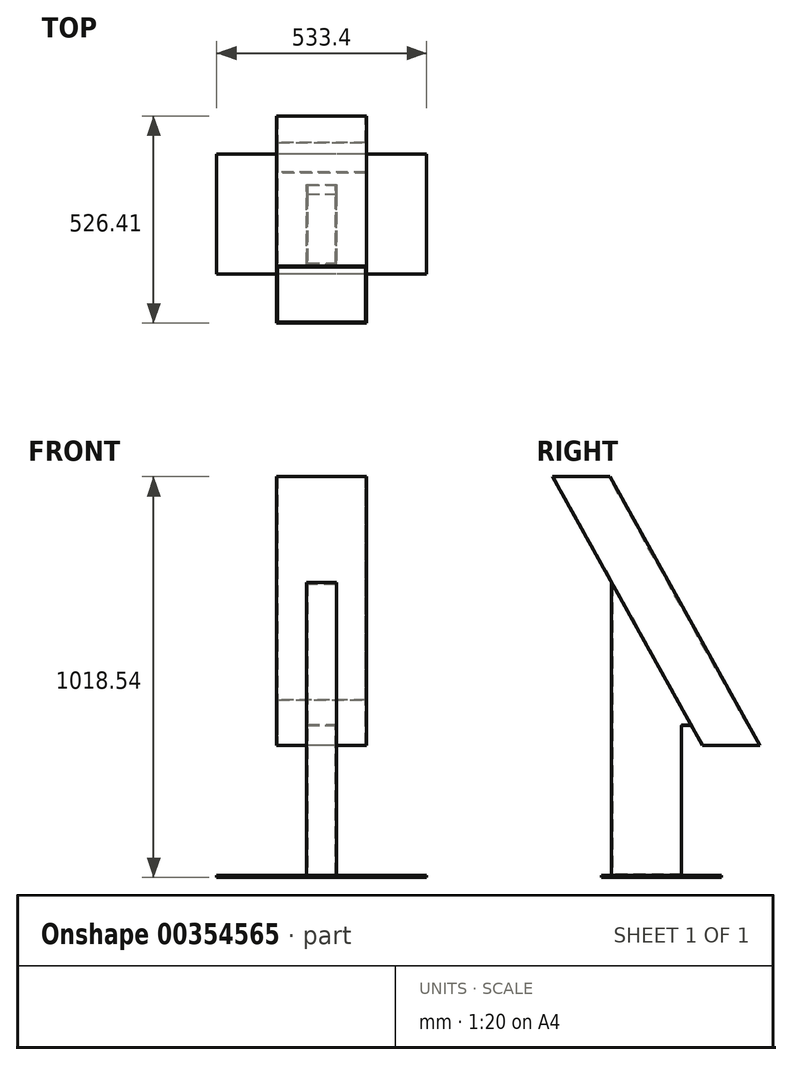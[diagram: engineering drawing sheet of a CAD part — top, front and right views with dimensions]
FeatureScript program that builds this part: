
annotation { "Feature Type Name" : "Feature", "Feature Type Description" : "" }
export const myFeature = defineFeature(function(context is Context, id is Id, definition is map)
    precondition{}
    {
        {
            var Q0;
            Q0=qCreatedBy(makeId("Right.planeOp"),FACE);
            var sketch = newSketch(context, id + "F0", { "sketchPlane" : qUnion([Q0])});
            skLineSegment(sketch, "E0", {"start": v(0, 0) * mm, "end": v(145.41, 0) * mm});
            skLineSegment(sketch, "E1", {"start": v(145.41, 0) * mm, "end": v(-235.59, 683.26) * mm});
            skLineSegment(sketch, "E2", {"start": v(-235.59, 683.26) * mm, "end": v(-381, 683.26) * mm});
            skLineSegment(sketch, "E3", {"start": v(-381, 683.26) * mm, "end": v(0, 0) * mm});
            skSolve(sketch);
        }
        {
            var Q0;
            Q0=makeQuery(id+"F0.imprint","IMPRINT",FACE,{"disambiguationData":[TD([[makeQuery(id+"F0.imprint","IMPRINT",EDGE,{"derivedFrom":sQuery(id+"F0.wireOp",EDGE,"qrRVfToE-z7uB-ETNp-0GDO-vOTHaiqZA0hq")}),1.0]])]});
            var Q1;
            Q1=makeQuery(id+"F0.imprint","IMPRINT",FACE,{"disambiguationData":[TD([[makeQuery(id+"F0.imprint","IMPRINT",EDGE,{"derivedFrom":sQuery(id+"F0.wireOp",EDGE,"E0")}),1.0]])]});
            extrude(context, id + "F1", {"entities" : qUnion([Q0, Q1]), "depth" : 228.6 * mm});
        }
        {
            var Q0;
            Q0=makeQuery(id+"F1.opExtrude","SWEPT_FACE",FACE,{"disambiguationData":[OSD([sQuery(id+"F0.wireOp",EDGE,"X73UDyVE-wi7P-lukd-QKiW-U0VLPajjbVpl")])]});
            var Q1;
            Q1=makeQuery(id+"F1.opExtrude","SWEPT_FACE",FACE,{"disambiguationData":[OSD([sQuery(id+"F0.wireOp",EDGE,"E2")])]});
            shell(context, id + "F2", {"entities" : qUnion([Q0, Q1]), "thickness" : 2.54 * mm});
        }
        {
            var Q0;
            Q0=makeQuery(id+"F1.opExtrude","SWEPT_EDGE",EDGE,{"disambiguationData":[OSD([sQuery(id+"F0.wireOp",EDGE,"E0"),sQuery(id+"F0.wireOp",EDGE,"E1")])]});
            cPlane(context, id + "F3", {"entities" : qUnion([Q0]), "cplaneType" : CPlaneType.LINE_ANGLE, "offset" : 25.4 * mm, "angle" : 60.86 * degree, "width" : 152.4 * mm, "height" : 152.4 * mm});
        }
        {
            var Q0;
            Q0=qCreatedBy(id+"F3.planeOp",FACE);
            var sketch = newSketch(context, id + "F4", { "sketchPlane" : qUnion([Q0])});
            skLineSegment(sketch, "E4.bottom", {"start": v(2.54, 2.54) * mm, "end": v(226.06, 2.54) * mm});
            skLineSegment(sketch, "E4.top", {"start": v(2.54, 124.47) * mm, "end": v(226.06, 124.47) * mm});
            skLineSegment(sketch, "E4.left", {"start": v(2.54, 2.54) * mm, "end": v(2.54, 124.47) * mm});
            skLineSegment(sketch, "E4.right", {"start": v(226.06, 2.54) * mm, "end": v(226.06, 124.47) * mm});
            skSolve(sketch);
        }
        {
            var Q0;
            Q0=makeQuery(id+"F4.imprint","IMPRINT",FACE,{"disambiguationData":[TD([[makeQuery(id+"F4.imprint","IMPRINT",EDGE,{"derivedFrom":sQuery(id+"F4.wireOp",EDGE,"E4.bottom")}),1.0]])]});
            extrude(context, id + "F5", {"entities" : qUnion([Q0]), "operationType" : NewBodyOperationType.REMOVE, "depth" : 134.11 * mm});
        }
        {
            var Q0;
            Q0=qCreatedBy(makeId("Front.planeOp"),FACE);
            cPlane(context, id + "F6", {"entities" : qUnion([Q0]), "cplaneType" : CPlaneType.OFFSET, "offset" : 231.14 * mm, "width" : 152.4 * mm, "height" : 152.4 * mm});
        }
        {
            var Q0;
            Q0=qCreatedBy(id+"F6.planeOp",FACE);
            var sketch = newSketch(context, id + "F7", { "sketchPlane" : qUnion([Q0])});
            skLineSegment(sketch, "E5.bottom", {"start": v(76.2, 228.6) * mm, "end": v(152.4, 228.6) * mm});
            skLineSegment(sketch, "E5.top", {"start": v(76.2, 50.8) * mm, "end": v(152.4, 50.8) * mm});
            skLineSegment(sketch, "E5.left", {"start": v(76.2, 228.6) * mm, "end": v(76.2, 50.8) * mm});
            skLineSegment(sketch, "E5.right", {"start": v(152.4, 228.6) * mm, "end": v(152.4, 50.8) * mm});
            skPoint(sketch, "E6", {"position": v(114.3, 50.8) * mm});
            skPoint(sketch, "E7", {"position": v(114.3, 228.6) * mm});
            skSolve(sketch);
        }
        {
            var Q0;
            Q0=makeQuery(id+"F7.imprint","IMPRINT",FACE,{"disambiguationData":[TD([[makeQuery(id+"F7.imprint","IMPRINT",EDGE,{"derivedFrom":sQuery(id+"F7.wireOp",EDGE,"E5.bottom")}),-1.0]])]});
            var Q1;
            Q1=makeQuery(id+"F1.opExtrude","SWEPT_FACE",FACE,{"disambiguationData":[OSD([sQuery(id+"F0.wireOp",EDGE,"E3")])]});
            extrude(context, id + "F8", {"entities" : qUnion([Q0]), "operationType" : NewBodyOperationType.ADD, "endBound" : BoundingType.UP_TO_SURFACE, "oppositeDirection" : true, "endBoundEntityFace" : qUnion([Q1]), "depth" : 25.4 * mm});
        }
        {
            var Q0;
            Q0=makeQuery(id+"F8.opExtrude","SWEPT_FACE",FACE,{"disambiguationData":[OSD([sQuery(id+"F7.wireOp",EDGE,"E5.top")])]});
            var sketch = newSketch(context, id + "F9", { "sketchPlane" : qUnion([Q0])});
            skLineSegment(sketch, "E8.bottom", {"start": v(76.2, 231.14) * mm, "end": v(152.4, 231.14) * mm});
            skLineSegment(sketch, "E8.top", {"start": v(76.2, 53.34) * mm, "end": v(152.4, 53.34) * mm});
            skLineSegment(sketch, "E8.left", {"start": v(76.2, 231.14) * mm, "end": v(76.2, 53.34) * mm});
            skLineSegment(sketch, "E8.right", {"start": v(152.4, 231.14) * mm, "end": v(152.4, 53.34) * mm});
            skSolve(sketch);
        }
        {
            var Q0;
            Q0=makeQuery(id+"F9.imprint","IMPRINT",FACE,{"disambiguationData":[TD([[makeQuery(id+"F9.imprint","IMPRINT",EDGE,{"derivedFrom":sQuery(id+"F9.wireOp",EDGE,"E8.bottom")}),-1.0]])]});
            extrude(context, id + "F10", {"entities" : qUnion([Q0]), "operationType" : NewBodyOperationType.ADD, "depth" : 381 * mm});
        }
        {
            var Q0;
            Q0=makeQuery(id+"F10.opExtrude","CAP_FACE",FACE,{"disambiguationData":[OSD([sQuery(id+"F9.wireOp",EDGE,"E8.bottom"),sQuery(id+"F9.wireOp",EDGE,"E8.top"),sQuery(id+"F9.wireOp",EDGE,"E8.left"),sQuery(id+"F9.wireOp",EDGE,"E8.right")])],"isStart":false});
            var sketch = newSketch(context, id + "F11", { "sketchPlane" : qUnion([Q0])});
            skLineSegment(sketch, "E9.bottom", {"start": v(381, -48.26) * mm, "end": v(-152.4, -48.26) * mm});
            skLineSegment(sketch, "E9.top", {"start": v(381, 256.54) * mm, "end": v(-152.4, 256.54) * mm});
            skLineSegment(sketch, "E9.left", {"start": v(381, -48.26) * mm, "end": v(381, 256.54) * mm});
            skLineSegment(sketch, "E9.right", {"start": v(-152.4, -48.26) * mm, "end": v(-152.4, 256.54) * mm});
            skPoint(sketch, "E10", {"position": v(114.3, 256.54) * mm});
            skPoint(sketch, "E11", {"position": v(114.3, -48.26) * mm});
            skSolve(sketch);
        }
        {
            var Q0;
            Q0=makeQuery(id+"F8.opExtrude","SWEPT_FACE",FACE,{"disambiguationData":[OSD([sQuery(id+"F7.wireOp",EDGE,"E5.bottom")])]});
            var Q1;
            Q1=makeQuery(id+"F1.opExtrude","SWEPT_FACE",FACE,{"disambiguationData":[OSD([sQuery(id+"F0.wireOp",EDGE,"E3")])]});
            extrude(context, id + "F12", {"entities" : qUnion([Q0]), "operationType" : NewBodyOperationType.ADD, "endBound" : BoundingType.UP_TO_SURFACE, "endBoundEntityFace" : qUnion([Q1]), "depth" : 25.4 * mm});
        }
        {
            var Q0;
            Q0=makeQuery(id+"F10.opExtrude","SWEPT_FACE",FACE,{"disambiguationData":[OSD([sQuery(id+"F9.wireOp",EDGE,"E8.top")])]});
            shell(context, id + "F13", {"entities" : qUnion([Q0]), "thickness" : 2.54 * mm});
        }
        {
            var Q0;
            Q0=makeQuery(id+"F11.imprint","IMPRINT",FACE,{"disambiguationData":[TD([[makeQuery(id+"F11.imprint","IMPRINT",EDGE,{"derivedFrom":sQuery(id+"F11.wireOp",EDGE,"E9.bottom")}),-1.0]])]});
            var Q1;
            Q1=makeQuery(id+"F11.imprint","IMPRINT",FACE,{"disambiguationData":[TD([[makeQuery(id+"F11.imprint","IMPRINT",EDGE,{"derivedFrom":makeQuery(id+"F10.opExtrude","CAP_EDGE",EDGE,{"disambiguationData":[OSD([sQuery(id+"F9.wireOp",EDGE,"E8.bottom")])],"isStart":false})}),-1.0]])]});
            extrude(context, id + "F14", {"entities" : qUnion([Q0, Q1]), "operationType" : NewBodyOperationType.ADD, "depth" : 5.08 * mm});
        }
    });
